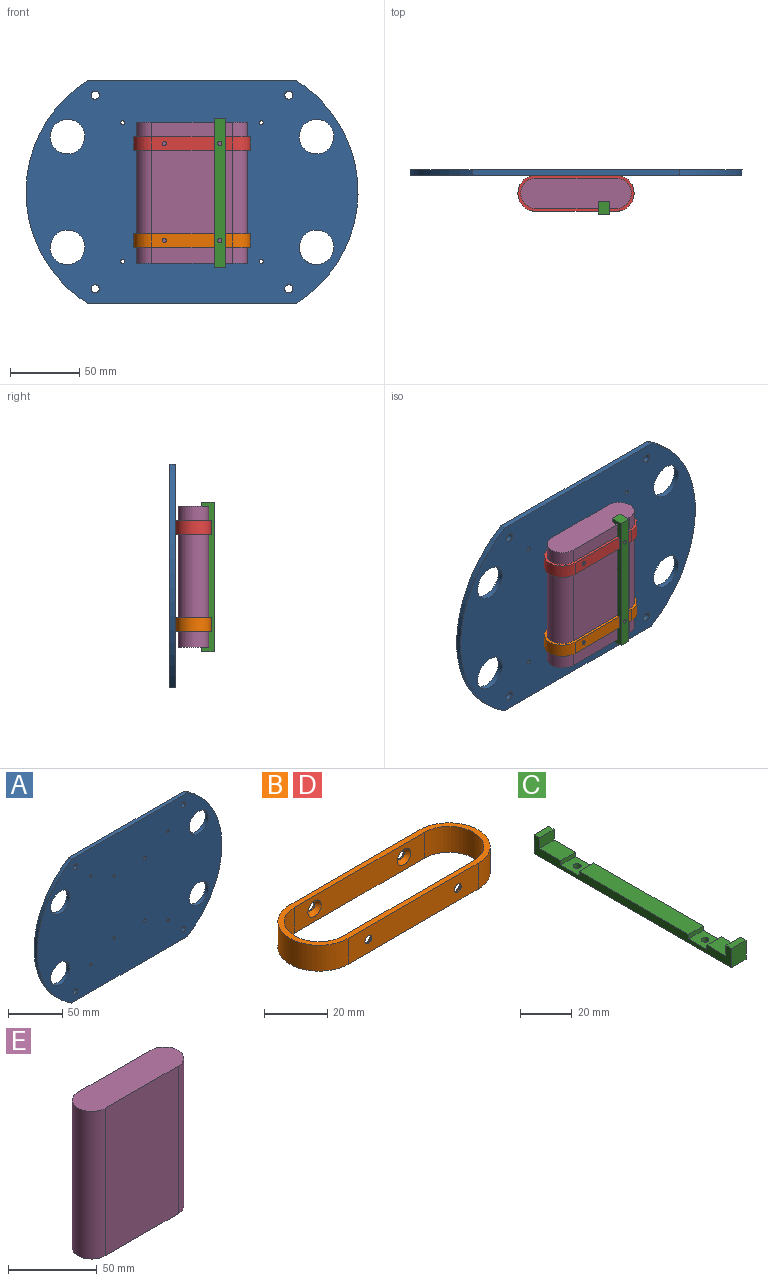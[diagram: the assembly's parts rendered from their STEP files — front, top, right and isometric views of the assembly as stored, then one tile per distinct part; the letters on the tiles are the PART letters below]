
ASSEMBLY  parts=5 mates=12
PART A: 30 faces, bbox 241.5x4x161.6 mm
  f0: cylinder r=12.5mm len=25mm, axis (0,1,0), area 157.1mm2, adj f1,f18,f20
  f1: cylinder r=12.5mm len=25mm, axis (0,1,0), area 157.1mm2, adj f0,f18,f20
  f2: cylinder r=12.5mm len=25mm, axis (0,1,0), area 157.1mm2, adj f3,f18,f20
  f3: cylinder r=12.5mm len=25mm, axis (0,1,0), area 157.1mm2, adj f2,f18,f20
  f4: cylinder r=12.5mm len=25mm, axis (0,1,0), area 157.1mm2, adj f5,f18,f20
  f5: cylinder r=12.5mm len=25mm, axis (0,1,0), area 157.1mm2, adj f4,f18,f20
  f6: cylinder r=3mm len=6mm, axis (0,1,0), area 37.7mm2, adj f7,f18,f20
  f7: cylinder r=3mm len=6mm, axis (0,1,0), area 37.7mm2, adj f6,f18,f20
  f8: cylinder r=3mm len=6mm, axis (0,1,0), area 37.7mm2, adj f9,f18,f20
  f9: cylinder r=3mm len=6mm, axis (0,1,0), area 37.7mm2, adj f8,f18,f20
  f10: cylinder r=3mm len=6mm, axis (0,1,0), area 37.7mm2, adj f11,f18,f20
  f11: cylinder r=3mm len=6mm, axis (0,1,0), area 37.7mm2, adj f10,f18,f20
  f12: cylinder r=3mm len=6mm, axis (0,1,0), area 37.7mm2, adj f13,f18,f20
  f13: cylinder r=3mm len=6mm, axis (0,1,0), area 37.7mm2, adj f12,f18,f20
  f14: cylinder r=95mm len=161.56mm, axis (0,1,0), area 772.6mm2, adj f15,f17,f18,f20
  f15: plane 150x4mm, normal (0,0,-1), area 600mm2, adj f14,f16,f18,f20
  f16: cylinder r=95mm len=161.56mm, axis (0,1,0), area 772.6mm2, adj f15,f17,f18,f20
  f17: plane 150x4mm, normal (0,0,1), area 600mm2, adj f14,f16,f18,f20
  f18: plane 241.47x161.56mm, normal (0,-1,0), area 32370.8mm2, adj f0,f1,f2,f3,f4,f5,f6,f7
  f19: cylinder r=12.5mm len=25mm, axis (0,1,0), area 157.1mm2, adj f18,f20,f21
  f20: plane 241.47x161.56mm, normal (0,1,0), area 32370.8mm2, adj f0,f1,f2,f3,f4,f5,f6,f7
  f21: cylinder r=12.5mm len=25mm, axis (0,1,0), area 157.1mm2, adj f18,f19,f20
  f22: cylinder r=1.5mm len=4mm, axis (0,-1,0), area 37.7mm2, adj f18,f20
  f23: cylinder r=1.5mm len=4mm, axis (0,-1,0), area 37.7mm2, adj f18,f20
  f24: cylinder r=1.5mm len=4mm, axis (0,-1,0), area 37.7mm2, adj f18,f20
  f25: cylinder r=1.5mm len=4mm, axis (0,-1,0), area 37.7mm2, adj f18,f20
  f26: cylinder r=1.5mm len=4mm, axis (0,-1,0), area 37.7mm2, adj f18,f20
  f27: cylinder r=1.5mm len=4mm, axis (0,-1,0), area 37.7mm2, adj f18,f20
  f28: cylinder r=1.5mm len=4mm, axis (0,-1,0), area 37.7mm2, adj f18,f20
  f29: cylinder r=1.5mm len=4mm, axis (0,-1,0), area 37.7mm2, adj f18,f20
PART B: 18 faces, bbox 84x26x10 mm
  f0: cylinder r=13mm len=26mm, axis (0,0,-1), area 408.4mm2, adj f1,f7,f8,f9
  f1: plane 58x10mm, normal (0,1,0), area 565.9mm2, adj f0,f2,f8,f9,f11,f13
  f2: cylinder r=13mm len=26mm, axis (0,0,-1), area 408.4mm2, adj f1,f7,f8,f9
  f3: plane 58x10mm, normal (0,-1,0), area 523.5mm2, adj f4,f6,f8,f9,f14,f15
  f4: cylinder r=11mm len=22mm, axis (0,0,-1), area 345.6mm2, adj f3,f5,f8,f9
  f5: plane 58x10mm, normal (0,1,0), area 523.5mm2, adj f4,f6,f8,f9,f16,f17
  f6: cylinder r=11mm len=22mm, axis (0,0,-1), area 345.6mm2, adj f3,f5,f8,f9
  f7: plane 58x10mm, normal (0,-1,0), area 565.9mm2, adj f0,f2,f8,f9,f10,f12
  f8: plane 84x26mm, normal (0,0,1), area 382.8mm2, adj f0,f1,f2,f3,f4,f5,f6,f7
  f9: plane 84x26mm, normal (0,0,-1), area 382.8mm2, adj f0,f1,f2,f3,f4,f5,f6,f7
  f10: cylinder r=1.5mm len=3mm, axis (0,-1,0), area 4.7mm2, adj f7,f16
  f11: cylinder r=1.5mm len=3mm, axis (0,-1,0), area 4.7mm2, adj f1,f14
  f12: cylinder r=1.5mm len=3mm, axis (0,-1,0), area 4.7mm2, adj f7,f17
  f13: cylinder r=1.5mm len=3mm, axis (0,-1,0), area 4.7mm2, adj f1,f15
  f14: cone r=1.5mm half-angle=45deg, axis (0,-1,0), area 30mm2, adj f3,f11
  f15: cone r=1.5mm half-angle=45deg, axis (0,-1,0), area 30mm2, adj f3,f13
  f16: cone r=3mm half-angle=45deg, axis (0,1,0), area 30mm2, adj f5,f10
  f17: cone r=3mm half-angle=45deg, axis (0,1,0), area 30mm2, adj f5,f12
PART C: 20 faces, bbox 8x108x9 mm
  f0: plane 60x8mm, normal (0,0,1), area 480mm2, adj f2,f6,f14,f17
  f1: plane 11.63x8mm, normal (0,0,1), area 93.1mm2, adj f2,f6,f10,f15
  f2: plane 108x9mm, normal (1,0,0), area 422mm2, adj f0,f1,f5,f7,f8,f9,f10,f11
  f3: cylinder r=1.5mm len=3mm, axis (0,0,1), area 18.8mm2, adj f9,f16
  f4: cylinder r=1.5mm len=3mm, axis (0,0,1), area 18.8mm2, adj f9,f19
  f5: plane 10.37x8mm, normal (0,0,1), area 82.9mm2, adj f2,f6,f12,f18
  f6: plane 108x9mm, normal (-1,0,0), area 422mm2, adj f0,f1,f5,f7,f8,f9,f10,f11
  f7: plane 9x8mm, normal (0,-1,0), area 72mm2, adj f2,f6,f9,f13
  f8: plane 9x8mm, normal (0,1,0), area 72mm2, adj f2,f6,f9,f11
  f9: plane 108x8mm, normal (0,0,-1), area 849.9mm2, adj f2,f3,f4,f6,f7,f8
  f10: plane 8x5mm, normal (0,-1,0), area 40mm2, adj f1,f2,f6,f11
  f11: plane 8x3mm, normal (0,0,1), area 24mm2, adj f2,f6,f8,f10
  f12: plane 8x5mm, normal (0,1,0), area 40mm2, adj f2,f5,f6,f13
  f13: plane 8x3mm, normal (0,0,1), area 24mm2, adj f2,f6,f7,f12
  f14: plane 8x2mm, normal (0,1,0), area 16mm2, adj f0,f2,f6,f16
  f15: plane 8x2mm, normal (0,-1,0), area 16mm2, adj f1,f2,f6,f16
  f16: plane 10x8mm, normal (0,0,1), area 72.9mm2, adj f2,f3,f6,f14,f15
  f17: plane 8x2mm, normal (0,-1,0), area 16mm2, adj f0,f2,f6,f19
  f18: plane 8x2mm, normal (0,1,0), area 16mm2, adj f2,f5,f6,f19
  f19: plane 10x8mm, normal (0,0,1), area 72.9mm2, adj f2,f4,f6,f17,f18
PART D: same geometry as B
PART E: 6 faces, bbox 80x22x102 mm
  f0: cylinder r=11mm len=102mm, axis (0,0,-1), area 3524.9mm2, adj f1,f3,f4,f5
  f1: plane 102x58mm, normal (0,-1,0), area 5916mm2, adj f0,f2,f4,f5
  f2: cylinder r=11mm len=102mm, axis (0,0,-1), area 3524.9mm2, adj f1,f3,f4,f5
  f3: plane 102x58mm, normal (0,1,0), area 5916mm2, adj f0,f2,f4,f5
  f4: plane 80x22mm, normal (0,0,1), area 1656.1mm2, adj f0,f1,f2,f3
  f5: plane 80x22mm, normal (0,0,-1), area 1656.1mm2, adj f0,f1,f2,f3
PLACE A at identity fixed
PLACE B t=(0,-13,-35)mm
PLACE C rot(axis=(-1,0,0),90deg) t=(20,-26,-0.63)mm
PLACE D t=(0,-13,35)mm
PLACE E t=(0,-13,-0.63)mm
MATE planar B.f1 <-> A.f18  axis (0,1,0) through (0,0,-35)mm
MATE planar D.f1 <-> A.f18  axis (0,1,0) through (0,0,35)mm
MATE cylindrical A.f27 <-> D.f12  axis (0,-1,0) through (20,2,35)mm
MATE cylindrical B.f12 <-> A.f28  axis (0,-1,0) through (20,-0.25,-35)mm
MATE cylindrical E.f2 <-> D.f4  axis (0,0,-1) through (29,-13,-0.63)mm
MATE planar C.f0 <-> E.f1  axis (0,1,0) through (20,-24,0)mm
MATE cylindrical E.f0 <-> B.f6  axis (0,0,-1) through (-29,-13,-0.63)mm
MATE cylindrical D.f10 <-> A.f26  axis (0,-1,0) through (-20,-0.25,35)mm
MATE planar E.f4 <-> C.f12  axis (0,0,1) through (0,-13,50.37)mm
MATE cylindrical C.f3 <-> B.f12  axis (0,1,0) through (20,-27,-35)mm
MATE cylindrical B.f10 <-> A.f29  axis (0,-1,0) through (-20,-0.25,-35)mm
MATE cylindrical C.f4 <-> D.f12  axis (0,1,0) through (20,-27,35)mm
